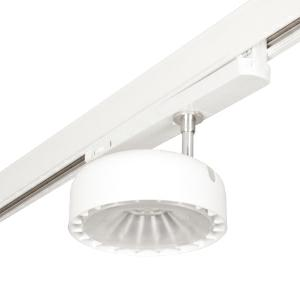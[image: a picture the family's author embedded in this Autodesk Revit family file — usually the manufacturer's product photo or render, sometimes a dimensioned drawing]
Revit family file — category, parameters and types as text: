
# Revit family: 3f_filippi_-_3f_emilio_track_ellittico_3f_filippi_-_47618_-_3f_emilio_tk_led_2000-930_ell
name_source: partatom
category: Lighting Fixtures
units: mm (PartAtom-declared; Revit-internal decimal feet)

## family parameters
Cut with Voids When Loaded = No
Host = Face
Light Source = No
Part Type = Normal
Room Calculation Point = No
Round Connector Dimension = Use Diameter
Shared = No

## types (1)
- 3F Filippi - 3F Emilio Track Ellittico (1 x LED, 2571 lm, 29 W, 3000 K)
    Apparent Load = 29 VA
    Approval mark = CE
    CIE Flux Codes = 85 95 99 100 100
    Color Rendering = 90
    Color Temperature = 3000 K
    Control Gear = Electronic ballast
    Default Elevation = 1800 mm
    Description = Adjustable spot light with minimal dimensions for accent lighting, to be integrated into the busbar.

ILLUMINOTECHNICAL
Luminous efficiency 100% (DLOR 100%, ULOR 0%).
Initial luminous flux of the luminaire 2571 lm.
Symmetrical and elliptical distribution.
Tabular UGR (CIE 117 - 4H-8H; S=0.25H; 70/50/20): RUG 20.8 - 25.4.
Beam angle: 42° - 87°.
Luminous efficacy 89 lm/W.
Lifetime (L90/B20): 30000 h. (tq+25°C)
Lifetime (L80/B20): 50000 h. (tq+25°C)
Sudden decreased luminous flux after 50000 hours: 0% (C0).
Photobiological safety in compliance with IEC/TR 62778: RG1 low risk, (IEC 62471).
In compliance with IEC/EN 62722-2-1 - IEC/EN 62717 standards.

SOURCE
Compact LED module 2000/930.
Energy efficiency class (UE 2019/2020 - UE 2019/2015): E.
CIE 13.3 Colour rendering index: CRI >90 (R9 >50%).
IES TM-30 Fidelity Index: Rf = 92 Rg = 101.
CCT nominal colour temperature 3000 K.
Colour initial tolerance (MacAdam): SDCM 3.
Zhaga Book 3 compliant.

MECHANICAL
Wired unit in white polycarbonate with busbar adaptor.
Single-piece in die-cast aluminium with passive dissipation, white colour, with perimeter cooling slots on upper edge, giving a crown of light effect to the fitting.
Invisible lock for positioning the luminous flux.
Lens made from transparent methacrylate (PMMA) with glossy surface and differentiated photo-etched.
Positioning arm in galvanised brass with sphere to allow for vertical positioning at angles from 0° to 90° and horizontal positioning from 0° to 290°.
Dimensions: diameter 130 mm, length 230 mm, height 105 mm. Weight 0.815 kg.
IP20 protection degree.
Glow-wire test resistance 650°C.

ELECTRICAL
Wiring unit separate from the body, invisible and integrated into the busbar.
Halogen Free electronic wiring 230V-50/60Hz, power factor 0.95, THD <25%, constant output current, SELV, class II, 1 driver.
Power of the luminaire 29 W.
ENEC - CE.
SAFE FLICKER: PstLM=<1 and SVM=<0.4 (IEC TR 61547-1 and IEC TR 63158), to ensure a more comfortable and safe light.
Ambient temperature from 0°C to +25°C.
Temperature class T6 max 85°C.
Relative humidity UR: <85%.

INSTALLATION
Track.

APPLICATIONS
Transit areas, spotlighting in commercial environments, exhibition areas, restaurants, shops and shop windows.

WARNING
Luminaire designed for disposal/recycling at end-of-life.
Replaceable (LED only) light source by a professional. Replaceable control gear by a professional.
    Height = 105 mm
    Lamp = 1 x LED
    Lamp Light Flux = 2571 lm
    Lamp Power = 29 W
    Lamp count = 1
    Length = 230 mm
    Lifetime = 50000 h
    Luminous efficacy = 89 lm/W
    Manufacturer = 3F Filippi
    ModVariant = No
    Model = 3F Filippi - 47618 - 3F Emilio TK LED 2000-930 ELL
    Mounting Place = Ceiling
    Mounting Type = Rail mounted
    Number of Poles = 1
    OnlyDefault = Yes
    Power Factor = 1
    Product Name = 3F Filippi - 3F Emilio Track Ellittico
    Product group = track mounted spotlight
    ProductGroupID = 12
    Protection Class = Protection class II
    Protection Degree = IP 20
    RLX_Detail_Level = 1
    RLX_Emergency_Light_Flux = 0 lm
    RLX_Emergency_Type = 0
    RLX_Emergency_Type_DB = No
    RlxData = <blob elided: 152813 chars, md5=19798c7e>
    Socket = socket
    Standby Power = 0 W
    System Light Flux = 2571 lm
    System Power = 29 W
    Type Comments = Product without accessories
    Type Image = 3ffilippi_47618.jpg
    URL = http://relux.com
    VarID = ---
    Voltage = 0 V
    Weight = 0.00 kg
    Width = 130 mm

## geometry (parser evidence)
native form markers: Blend x4, Sweep x16
no freeform markers — native parametric forms only
